# Revit family: 303_R415PX_+R470
name_source: partatom
category: Pipe Accessories
revit_build: Autodesk Revit 2018 (Build: 20170223_1515(x64)
units: mm (PartAtom-declared; Revit-internal decimal feet)

## family parameters
Always vertical = Yes
Cut with Voids When Loaded = No
Part Type = Valve - Breaks Into
Round Connector Dimension = Use Diameter
Shared = No
Work Plane-Based = No

## types (1)
- R415PX042+R470
    CAT0 = Yes
    CenSd_K1_6 = 7 mm  [stored 0.0229659 ft]
    CenSd_W3_6 = 13 mm
    D = 16 mm
    D1 = 15 mm
    Description = Angle valve with precision adjustment numberscale and protection cap
    G1 = 9 mm  [stored 0.0295276 ft]
    J = 36 mm  [stored 0.11811 ft]
    J1 = 7 mm  [stored 0.0229659 ft]
    J2 = 5 mm  [stored 0.0164042 ft]
    J3 = 23 mm
    K1 = 8 mm  [stored 0.0262467 ft]
    K2 = 6 mm  [stored 0.019685 ft]
    L1 = 9 mm  [stored 0.0295276 ft]
    L2 = 17 mm  [stored 0.0557743 ft]
    L2D = 34 mm  [stored 0.111549 ft]
    L2D_Min = 3048 mm  [stored 10 ft]
    L5 = 11 mm
    L6 = 6 mm  [stored 0.019685 ft]
    LT1 = 19 mm
    LT1__ve = -19 mm
    MC_Default_elevation = 0 mm  [stored 0 ft]
    Manufacturer = Giacomini
    P1 = Yes
    P2 = No
    QmdConnectorList = 301;D;302;D1
    R = 8 mm  [stored 0.0262467 ft]
    TH2 = 82 mm
    TH2__ve = -82 mm
    TR1 = 20 mm  [stored 0.0656168 ft]
    URL = http://www.giacomini.com
    W1 = 5 mm  [stored 0.0164042 ft]
    W2 = 12 mm  [stored 0.0393701 ft]
    W2D = 16 mm  [stored 0.0524934 ft]
    W3 = 15 mm  [stored 0.0492126 ft]
    W4 = 8 mm  [stored 0.0262467 ft]
    Z1 = 10 mm  [stored 0.0328084 ft]
    magiPartTypeId = 303
    magiProductCode = R415PX042+R470
    magiProductFamilyId = R415PX*+R470
    magiProductId = R415PX042+R470

note: [stored X ft] marks values corroborated as IEEE doubles in the binary element streams (Revit-internal decimal feet)

## geometry (parser evidence)
native form markers: Sweep x1
no freeform markers — native parametric forms only
